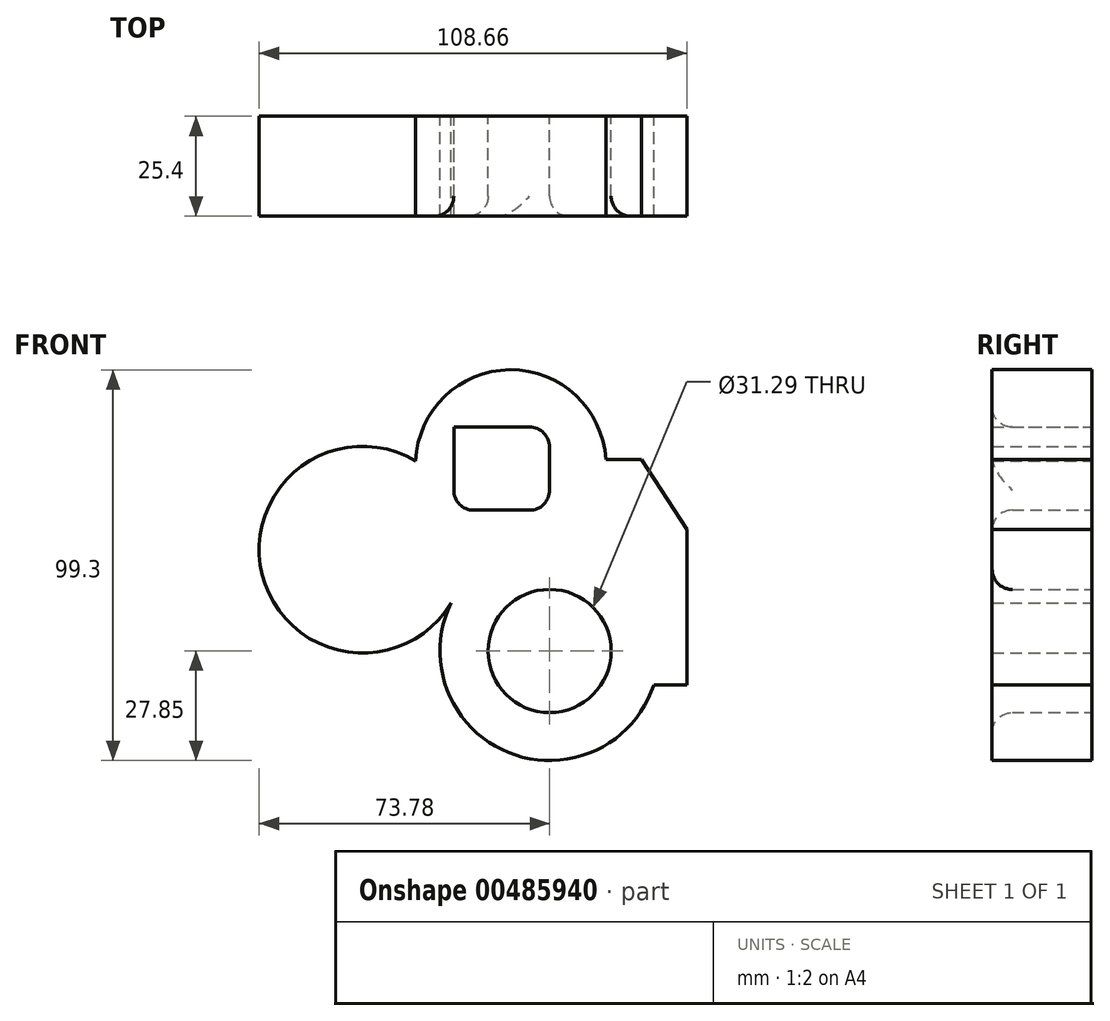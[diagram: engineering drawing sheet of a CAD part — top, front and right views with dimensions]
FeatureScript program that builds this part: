
annotation { "Feature Type Name" : "Feature", "Feature Type Description" : "" }
export const myFeature = defineFeature(function(context is Context, id is Id, definition is map)
    precondition{}
    {
        {
            var Q0;
            Q0=qCreatedBy(makeId("Front.planeOp"),FACE);
            var sketch = newSketch(context, id + "F0", { "sketchPlane" : qUnion([Q0])});
            skArc(sketch, "E0", {"start": v(14.27, 48.65) * mm, "mid": v(-10.06, 71.45) * mm, "end": v(-34.02, 48.27) * mm});
            skLineSegment(sketch, "E1.bottom", {"start": v(14.27, 48.65) * mm, "end": v(23.35, 48.65) * mm});
            skLineSegment(sketch, "E1.top", {"start": v(26.49, -8.6) * mm, "end": v(34.88, -8.6) * mm});
            skArc(sketch, "E2", {"start": v(-23.9, 14.3) * mm, "mid": v(-27.83, -0.94) * mm, "end": v(-22.87, -15.9) * mm});
            skArc(sketch, "E3", {"start": v(-22.87, -15.9) * mm, "mid": v(-4.03, -27.55) * mm, "end": v(17.36, -21.77) * mm});
            skArc(sketch, "E4", {"start": v(17.36, -21.77) * mm, "mid": v(22.9, -15.86) * mm, "end": v(26.49, -8.6) * mm});
            skLineSegment(sketch, "E5", {"start": v(34.88, 30.87) * mm, "end": v(34.88, -8.6) * mm});
            skArc(sketch, "E6", {"start": v(-34.02, 48.27) * mm, "mid": v(-72.69, 18.25) * mm, "end": v(-23.9, 14.3) * mm});
            skLineSegment(sketch, "E7", {"start": v(23.35, 48.65) * mm, "end": v(34.88, 30.87) * mm});
            skSolve(sketch);
        }
        {
            var Q0;
            Q0 = qSketchRegion(id + "F0", true);
            extrude(context, id + "F1", {"entities" : qUnion([Q0]), "endBound" : BoundingType.SYMMETRIC, "depth" : 25.4 * mm, "offsetDistance" : 25.4 * mm});
        }
        {
            var Q0;
            Q0=makeQuery(id+"F1.opExtrude","CAP_FACE",FACE,{"disambiguationData":[OSD([sQuery(id+"F0.wireOp",EDGE,"E0"),sQuery(id+"F0.wireOp",EDGE,"E1.bottom"),sQuery(id+"F0.wireOp",EDGE,"E1.top"),sQuery(id+"F0.wireOp",EDGE,"E2"),sQuery(id+"F0.wireOp",EDGE,"E3"),sQuery(id+"F0.wireOp",EDGE,"E4"),sQuery(id+"F0.wireOp",EDGE,"E5"),sQuery(id+"F0.wireOp",EDGE,"E6"),sQuery(id+"F0.wireOp",EDGE,"E7")])],"isStart":true});
            var sketch = newSketch(context, id + "F2", { "sketchPlane" : qUnion([Q0])});
            skCircle(sketch, "E8", {"center": v(0, 0) * mm, "radius": 15.64 * mm});
            skSolve(sketch);
        }
        {
            var Q0;
            Q0 = qSketchRegion(id + "F2", true);
            extrude(context, id + "F3", {"entities" : qUnion([Q0]), "operationType" : NewBodyOperationType.REMOVE, "endBound" : BoundingType.THROUGH_ALL, "oppositeDirection" : true, "depth" : 25.4 * mm, "offsetDistance" : 25.4 * mm});
        }
        {
            var Q0;
            Q0=makeQuery(id+"F3.boolean.opBoolean","COPY",EDGE,{"derivedFrom":makeQuery(id+"F3.opExtrude","CAP_EDGE",EDGE,{"disambiguationData":[OSD([sQuery(id+"F2.wireOp",EDGE,"E8")])],"isStart":true})});
            var Q1;
            Q1=makeQuery(id+"F3.boolean.opBoolean","INTERSECT",EDGE,{"derivedFrom":[makeQuery(id+"F1.opExtrude","CAP_FACE",FACE,{"disambiguationData":[OSD([sQuery(id+"F0.wireOp",EDGE,"E0"),sQuery(id+"F0.wireOp",EDGE,"E1.bottom"),sQuery(id+"F0.wireOp",EDGE,"E1.top"),sQuery(id+"F0.wireOp",EDGE,"E2"),sQuery(id+"F0.wireOp",EDGE,"E3"),sQuery(id+"F0.wireOp",EDGE,"E4"),sQuery(id+"F0.wireOp",EDGE,"E5"),sQuery(id+"F0.wireOp",EDGE,"E6"),sQuery(id+"F0.wireOp",EDGE,"E7")])],"isStart":false}),makeQuery(id+"F3.opExtrude","SWEPT_FACE",FACE,{"disambiguationData":[OSD([sQuery(id+"F2.wireOp",EDGE,"E8")])]})]});
            fillet(context, id + "F4", {"entities" : qUnion([Q0, Q1]), "radius" : 5.08 * mm, "tangentPropagation" : true, "allowEdgeOverflow" : false});
        }
        {
            var Q0;
            Q0=makeQuery(id+"F1.opExtrude","CAP_FACE",FACE,{"disambiguationData":[OSD([sQuery(id+"F0.wireOp",EDGE,"E0"),sQuery(id+"F0.wireOp",EDGE,"E1.bottom"),sQuery(id+"F0.wireOp",EDGE,"E1.top"),sQuery(id+"F0.wireOp",EDGE,"E2"),sQuery(id+"F0.wireOp",EDGE,"E3"),sQuery(id+"F0.wireOp",EDGE,"E4"),sQuery(id+"F0.wireOp",EDGE,"E5"),sQuery(id+"F0.wireOp",EDGE,"E6"),sQuery(id+"F0.wireOp",EDGE,"E7")])],"isStart":true});
            var sketch = newSketch(context, id + "F5", { "sketchPlane" : qUnion([Q0])});
            skLineSegment(sketch, "E9.bottom", {"start": v(24.34, 56.88) * mm, "end": v(0, 56.88) * mm});
            skLineSegment(sketch, "E9.top", {"start": v(24.34, 35.78) * mm, "end": v(0, 35.78) * mm});
            skLineSegment(sketch, "E9.left", {"start": v(24.34, 56.88) * mm, "end": v(24.34, 35.78) * mm});
            skLineSegment(sketch, "E9.right", {"start": v(0, 56.88) * mm, "end": v(0, 35.78) * mm});
            skSolve(sketch);
        }
        {
            var Q0;
            Q0 = qSketchRegion(id + "F5", true);
            extrude(context, id + "F6", {"entities" : qUnion([Q0]), "operationType" : NewBodyOperationType.REMOVE, "endBound" : BoundingType.THROUGH_ALL, "oppositeDirection" : true, "depth" : 25.4 * mm, "offsetDistance" : 25.4 * mm});
        }
        {
            var Q0;
            Q0=makeQuery(id+"F6.boolean.opBoolean","COPY",EDGE,{"derivedFrom":makeQuery(id+"F6.opExtrude","CAP_EDGE",EDGE,{"disambiguationData":[OSD([sQuery(id+"F5.wireOp",EDGE,"E9.right")])],"isStart":true})});
            var Q1;
            Q1=makeQuery(id+"F6.boolean.opBoolean","COPY",EDGE,{"derivedFrom":makeQuery(id+"F6.opExtrude","CAP_EDGE",EDGE,{"disambiguationData":[OSD([sQuery(id+"F5.wireOp",EDGE,"E9.left")])],"isStart":true})});
            var Q2;
            Q2=makeQuery(id+"F6.boolean.opBoolean","COPY",EDGE,{"derivedFrom":makeQuery(id+"F6.opExtrude","CAP_EDGE",EDGE,{"disambiguationData":[OSD([sQuery(id+"F5.wireOp",EDGE,"E9.top")])],"isStart":true})});
            var Q3;
            Q3=makeQuery(id+"F6.boolean.opBoolean","COPY",EDGE,{"derivedFrom":makeQuery(id+"F6.opExtrude","CAP_EDGE",EDGE,{"disambiguationData":[OSD([sQuery(id+"F5.wireOp",EDGE,"E9.bottom")])],"isStart":true})});
            var Q4;
            Q4=makeQuery(id+"F6.boolean.opBoolean","COPY",EDGE,{"derivedFrom":makeQuery(id+"F6.opExtrude","SWEPT_EDGE",EDGE,{"disambiguationData":[OSD([sQuery(id+"F5.wireOp",EDGE,"E9.bottom"),sQuery(id+"F5.wireOp",EDGE,"E9.right")])]})});
            var Q5;
            Q5=makeQuery(id+"F6.boolean.opBoolean","INTERSECT",EDGE,{"derivedFrom":[makeQuery(id+"F1.opExtrude","CAP_FACE",FACE,{"disambiguationData":[OSD([sQuery(id+"F0.wireOp",EDGE,"E0"),sQuery(id+"F0.wireOp",EDGE,"E1.bottom"),sQuery(id+"F0.wireOp",EDGE,"E1.top"),sQuery(id+"F0.wireOp",EDGE,"E2"),sQuery(id+"F0.wireOp",EDGE,"E3"),sQuery(id+"F0.wireOp",EDGE,"E4"),sQuery(id+"F0.wireOp",EDGE,"E5"),sQuery(id+"F0.wireOp",EDGE,"E6"),sQuery(id+"F0.wireOp",EDGE,"E7")])],"isStart":false}),makeQuery(id+"F6.opExtrude","SWEPT_FACE",FACE,{"disambiguationData":[OSD([sQuery(id+"F5.wireOp",EDGE,"E9.right")])]})]});
            var Q6;
            Q6=makeQuery(id+"F6.boolean.opBoolean","INTERSECT",EDGE,{"derivedFrom":[makeQuery(id+"F1.opExtrude","CAP_FACE",FACE,{"disambiguationData":[OSD([sQuery(id+"F0.wireOp",EDGE,"E0"),sQuery(id+"F0.wireOp",EDGE,"E1.bottom"),sQuery(id+"F0.wireOp",EDGE,"E1.top"),sQuery(id+"F0.wireOp",EDGE,"E2"),sQuery(id+"F0.wireOp",EDGE,"E3"),sQuery(id+"F0.wireOp",EDGE,"E4"),sQuery(id+"F0.wireOp",EDGE,"E5"),sQuery(id+"F0.wireOp",EDGE,"E6"),sQuery(id+"F0.wireOp",EDGE,"E7")])],"isStart":false}),makeQuery(id+"F6.opExtrude","SWEPT_FACE",FACE,{"disambiguationData":[OSD([sQuery(id+"F5.wireOp",EDGE,"E9.top")])]})]});
            var Q7;
            Q7=makeQuery(id+"F6.boolean.opBoolean","COPY",EDGE,{"derivedFrom":makeQuery(id+"F6.opExtrude","SWEPT_EDGE",EDGE,{"disambiguationData":[OSD([sQuery(id+"F5.wireOp",EDGE,"E9.top"),sQuery(id+"F5.wireOp",EDGE,"E9.right")])]})});
            var Q8;
            Q8=makeQuery(id+"F6.boolean.opBoolean","COPY",EDGE,{"derivedFrom":makeQuery(id+"F6.opExtrude","SWEPT_EDGE",EDGE,{"disambiguationData":[OSD([sQuery(id+"F5.wireOp",EDGE,"E9.top"),sQuery(id+"F5.wireOp",EDGE,"E9.left")])]})});
            fillet(context, id + "F7", {"entities" : qUnion([Q0, Q1, Q2, Q3, Q4, Q5, Q6, Q7, Q8]), "radius" : 5.08 * mm, "tangentPropagation" : true, "allowEdgeOverflow" : false});
        }
    });
